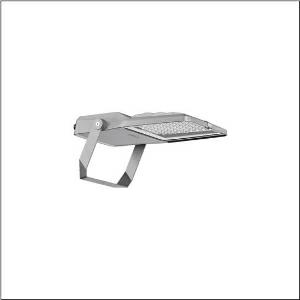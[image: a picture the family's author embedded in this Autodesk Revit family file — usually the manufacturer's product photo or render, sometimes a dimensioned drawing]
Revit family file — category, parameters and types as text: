
# Revit family: floodlight_fl_21_iq_mini___pl61_5xa7772c4c1a_7179
name_source: partatom
category: Lighting Fixtures
units: mm (PartAtom-declared; Revit-internal decimal feet)

## family parameters
Cut with Voids When Loaded = No
Host = Face
Light Source = No
Part Type = Normal
Room Calculation Point = No
Round Connector Dimension = Use Diameter
Shared = No

## types (1)
- --- (1 x LED, 12490 lm, 87.2 W, 4000K)
    Apparent Load = 87 VA
    CIE Flux Codes = 33 65 98 100 100
    Color Rendering = 70
    Color Temperature = 4000K
    Default Elevation = 1800 mm
    Description = Floodlight FL 21 iQ mini, floodlight, primary light control with lens, of PMMA, primary optical cover: protective disc, of toughened safety glass, transparent, light distribution: PL61, light emission: direct distribution, installation type: surface-mounted, LED, High Power LED, rated luminous flux: 12.490lm, luminous efficacy: 143lm/W, light colour: 740, colour temperature: 4000K, control gear: iQ Street-Remote/DALI, control: Street-Remote, Auto-Match, Temp-Guard, Night-Set, Smart-Wire, Desk-Remote (wireless, voltage-free reading and setting of iQ features in the workshop via application-optimized NFC function/RFID function), optimised constant luminous flux control (CLO 2.0), with terminal, 6-pole, mains connection: 220..240V, AC, 50/60Hz, start of lifetime: 87W, end of service life: 92W, reduction: 40W, luminaire housing, of diecast aluminium, powder-coated, Siteco® metallic grey (DB 702S), corrosivity category C5 mid according to DIN EN ISO 12944, suitable for swimming pools, chlorine-resistant, sealing non-destructively replaceable, mounting bracket, of steel, galvanised, powder-coated, Siteco® metallic grey (DB 702S), protection rating (complete): IP66, insulation class (complete): insulation class II (safety insulation), certification: CE, ENEC, VDE, protection symbol: D, impact resistance: IK08, permissible operating ambient temperature: -40..+40°C, permissible operating ambient temperature for outdoor applications: -40..+50°C, standard: DIN EN 12944, LABS conformity tested according to VDMA 24364:2018-05, packaging unit: 1 piece

Light Distribution: PL61
    Height = 70 mm
    Lamp = 1 x LED
    Lamp Light Flux = 12490 lm
    Lamp Power = 87.2 W
    Lamp count = 1
    Length = 485 mm
    Luminous efficacy = 143 lm/W
    Manufacturer = Siteco
    ModVariant = No
    Model = 5XA7772C4C1A
    Number of Poles = 1
    OnlyDefault = Yes
    Power Factor = 1
    Product Name = Floodlight FL 21 iQ mini | PL61
    Product group = floodlight | pylon annexe
    ProductGroupID = 6200
    Protection Class = Protection class II
    Protection Degree = IP 66
    RLX_Detail_Level = 1
    RLX_Emergency_Light_Flux = 0 lm
    RLX_Emergency_Type = 0
    RLX_Emergency_Type_DB = No
    RlxData = <blob elided: 96561 chars, md5=b1f82073>
    Socket = socket
    Standby Power = 0 W
    System Light Flux = 12490 lm
    System Power = 87 W
    Type Comments = factory setting: luminous flux: 100 % | dim-lin: 254 | 456 mA
    Type Image = l_1006845.jpg
    URL = http://relux.com
    VarID = @adj_172972
    Voltage = 0 V
    Weight = 0.00 kg
    Width = 337 mm

## geometry (parser evidence)
native form markers: Blend x4, Sweep x11
no freeform markers — native parametric forms only
